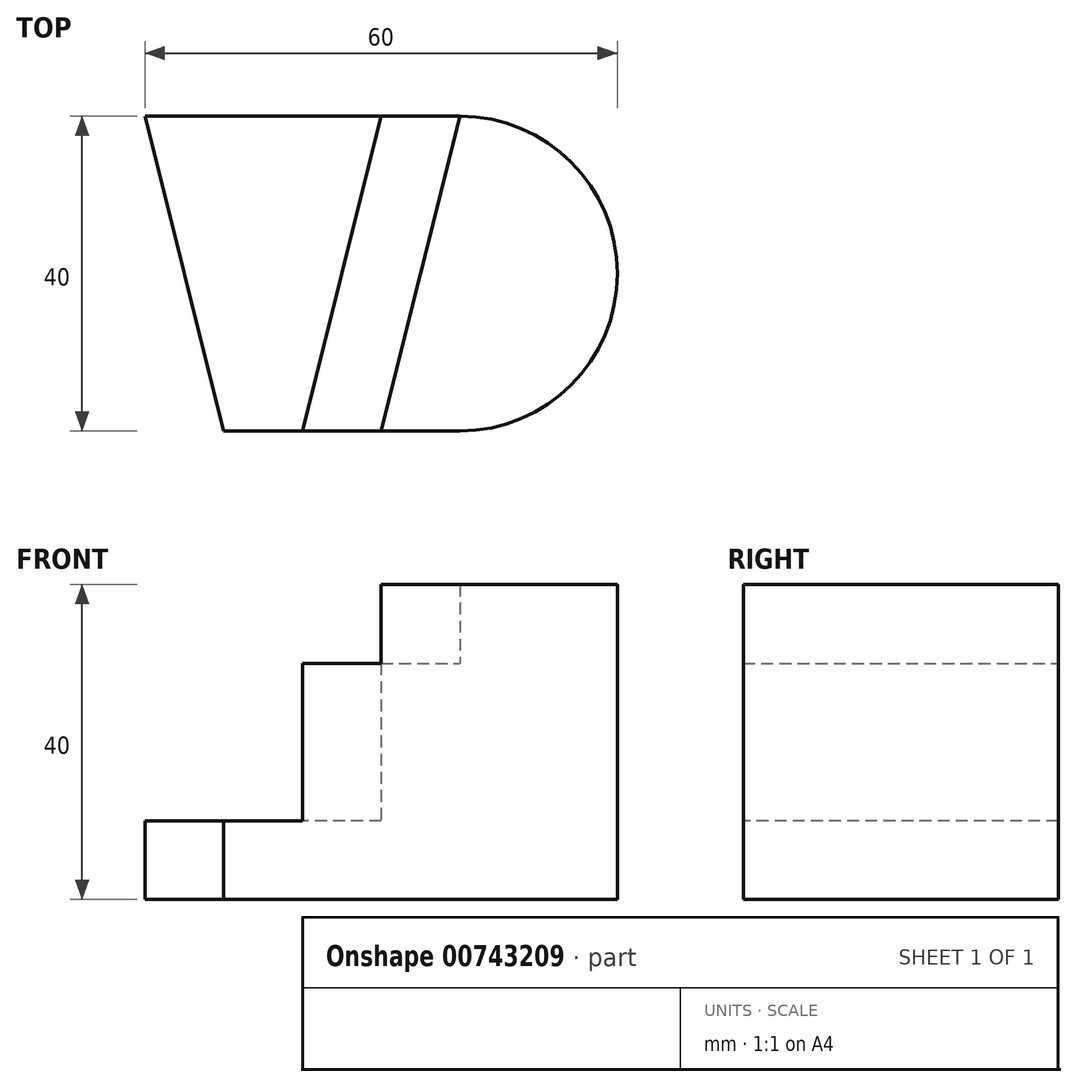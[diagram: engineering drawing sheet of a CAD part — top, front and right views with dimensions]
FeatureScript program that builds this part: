
annotation { "Feature Type Name" : "Feature", "Feature Type Description" : "" }
export const myFeature = defineFeature(function(context is Context, id is Id, definition is map)
    precondition{}
    {
        {
            var Q0;
            Q0=qCreatedBy(makeId("Top.planeOp"),FACE);
            var sketch = newSketch(context, id + "F0", { "sketchPlane" : qUnion([Q0])});
            skArc(sketch, "E0", {"start": v(0, -20) * mm, "mid": v(20, 0) * mm, "end": v(0, 20) * mm});
            skLineSegment(sketch, "E1", {"start": v(0, -20) * mm, "end": v(-10, -20) * mm});
            skLineSegment(sketch, "E2", {"start": v(-10, -20) * mm, "end": v(0, 20) * mm});
            skSolve(sketch);
        }
        {
            var Q0;
            Q0=makeQuery(id+"F0.imprint","IMPRINT",FACE,{"disambiguationData":[TD([[makeQuery(id+"F0.imprint","IMPRINT",EDGE,{"derivedFrom":sQuery(id+"F0.wireOp",EDGE,"E0")}),1.0]])]});
            extrude(context, id + "F1", {"entities" : qUnion([Q0]), "depth" : 40 * mm, "offsetDistance" : 25 * mm});
        }
        {
            var Q0;
            Q0=makeQuery(id+"F1.opExtrude","CAP_FACE",FACE,{"disambiguationData":[OSD([sQuery(id+"F0.wireOp",EDGE,"E0"),sQuery(id+"F0.wireOp",EDGE,"E1"),sQuery(id+"F0.wireOp",EDGE,"E2")])],"isStart":true});
            var sketch = newSketch(context, id + "F2", { "sketchPlane" : qUnion([Q0])});
            skLineSegment(sketch, "E3", {"start": v(0, -20) * mm, "end": v(-10, -20) * mm});
            skLineSegment(sketch, "E4", {"start": v(-10, -20) * mm, "end": v(-20, 20) * mm});
            skLineSegment(sketch, "E5", {"start": v(-20, 20) * mm, "end": v(-10, 20) * mm});
            skSolve(sketch);
        }
        {
            var Q0;
            Q0=makeQuery(id+"F2.imprint","IMPRINT",FACE,{"disambiguationData":[TD([[makeQuery(id+"F2.imprint","IMPRINT",EDGE,{"derivedFrom":sQuery(id+"F2.wireOp",EDGE,"E3")}),-1.0]])]});
            extrude(context, id + "F3", {"entities" : qUnion([Q0]), "operationType" : NewBodyOperationType.ADD, "oppositeDirection" : true, "depth" : 30 * mm, "offsetDistance" : 25 * mm});
        }
        {
            var Q0;
            {var subQ0=sQuery(id+"F0.wireOp",EDGE,"E2");Q0=makeQuery(id+"F3.boolean.opBoolean","MERGE",FACE,{"derivedFrom":[makeQuery(id+"F1.opExtrude","CAP_FACE",FACE,{"disambiguationData":[OSD([sQuery(id+"F0.wireOp",EDGE,"E0"),sQuery(id+"F0.wireOp",EDGE,"E1"),subQ0])],"isStart":true}),makeQuery(id+"F3.opExtrude","CAP_FACE",FACE,{"disambiguationData":[OSD([subQ0,sQuery(id+"F2.wireOp",EDGE,"E3"),sQuery(id+"F2.wireOp",EDGE,"E4"),sQuery(id+"F2.wireOp",EDGE,"E5")])],"isStart":true})]});}
            var sketch = newSketch(context, id + "F4", { "sketchPlane" : qUnion([Q0])});
            skLineSegment(sketch, "E6", {"start": v(-10, -20) * mm, "end": v(-20, 20) * mm});
            skLineSegment(sketch, "E7", {"start": v(-10, -20) * mm, "end": v(-40, -20) * mm});
            skLineSegment(sketch, "E8", {"start": v(-20, 20) * mm, "end": v(-30, 20) * mm});
            skLineSegment(sketch, "E9", {"start": v(-30, 20) * mm, "end": v(-40, -20) * mm});
            skSolve(sketch);
        }
        {
            var Q0;
            Q0=makeQuery(id+"F4.imprint","IMPRINT",FACE,{"disambiguationData":[TD([[makeQuery(id+"F4.imprint","IMPRINT",EDGE,{"derivedFrom":sQuery(id+"F4.wireOp",EDGE,"E6")}),1.0]])]});
            extrude(context, id + "F5", {"entities" : qUnion([Q0]), "operationType" : NewBodyOperationType.ADD, "oppositeDirection" : true, "depth" : 10 * mm, "offsetDistance" : 25 * mm});
        }
    });
